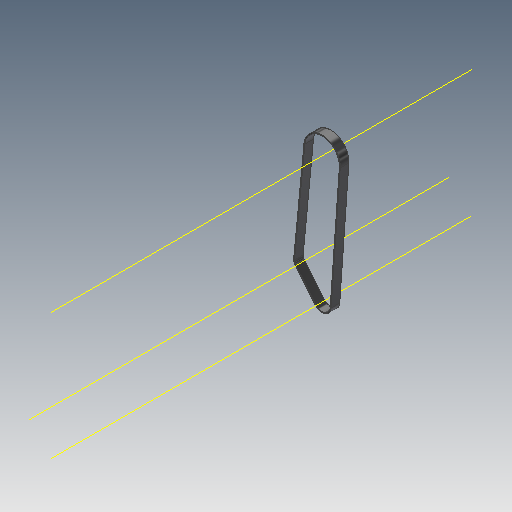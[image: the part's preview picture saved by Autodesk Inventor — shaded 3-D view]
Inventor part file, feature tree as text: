
AUTODESK INVENTOR PART (.ipt)
format: ipt  version: 2018 (Build 220112000, 112)  size: 104,960 bytes
history: native  units: mm (DEFAULTED — no unit token found)
features: other x5, plane x3, sketch x1, sweep x1
ambient origin geometry x8: Origin, YZ Plane, XZ Plane, XY Plane, X Axis, Y Axis, Z Axis, Center Point
bodies: Solid1 (feature_tree)
feature tree (10):
  sketch  "Sketch Path"  dims[d0=6.0mm d2=0.0mm d4=0.3mm d5=0.3mm d6=0.0mm d7=0.0mm d8=0.0mm d9=0.0mm d10=0.0mm d11=0.0mm d12=0.0mm d13=0.0mm]
  other  "Cross Section Plane"
  other  "Work Axis1"
  other  "Work Axis2"
  other  "Work Axis3"
  plane  "Work Plane2"
  plane  "Work Plane3"
  plane  "Work Plane4"
  sweep  "Belt"
  other  "Cross Section"
